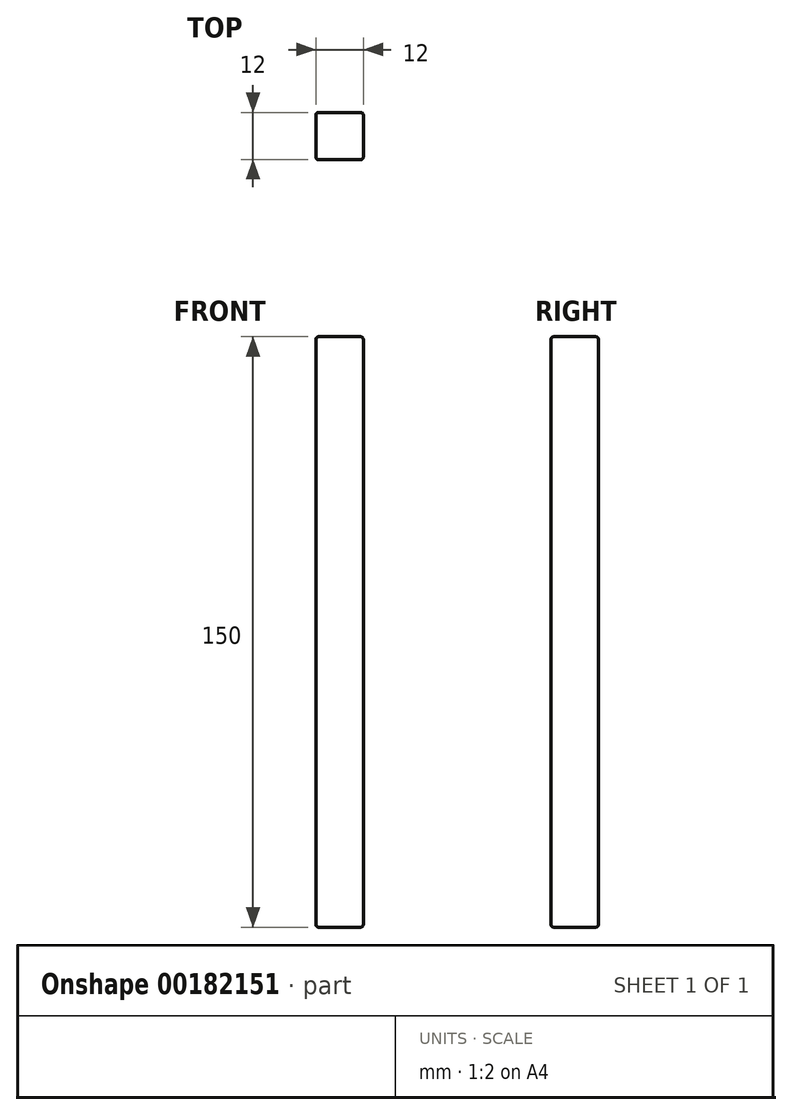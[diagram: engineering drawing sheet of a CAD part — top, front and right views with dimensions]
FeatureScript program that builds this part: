
annotation { "Feature Type Name" : "Feature", "Feature Type Description" : "" }
export const myFeature = defineFeature(function(context is Context, id is Id, definition is map)
    precondition{}
    {
        {
            var Q0;
            Q0=qCreatedBy(makeId("Top.planeOp"),FACE);
            var sketch = newSketch(context, id + "F0", { "sketchPlane" : qUnion([Q0])});
            skLineSegment(sketch, "E0.bottom", {"start": v(6, -6) * mm, "end": v(-6, -6) * mm});
            skLineSegment(sketch, "E0.top", {"start": v(6, 6) * mm, "end": v(-6, 6) * mm});
            skLineSegment(sketch, "E0.left", {"start": v(6, -6) * mm, "end": v(6, 6) * mm});
            skLineSegment(sketch, "E0.right", {"start": v(-6, -6) * mm, "end": v(-6, 6) * mm});
            skPoint(sketch, "E0.middle", {"position": v(0, 0) * mm});
            skSolve(sketch);
        }
        {
            var Q0;
            Q0 = qSketchRegion(id + "F0", true);
            extrude(context, id + "F1", {"entities" : qUnion([Q0]), "depth" : 150 * mm});
        }
        {
            var Q0;
            Q0=makeQuery(id+"F1.opExtrude","CAP_FACE",FACE,{"disambiguationData":[OSD([sQuery(id+"F0.wireOp",EDGE,"E0.bottom"),sQuery(id+"F0.wireOp",EDGE,"E0.top"),sQuery(id+"F0.wireOp",EDGE,"E0.left"),sQuery(id+"F0.wireOp",EDGE,"E0.right")])],"isStart":false});
            var Q1;
            Q1=makeQuery(id+"F1.opExtrude","SWEPT_FACE",FACE,{"disambiguationData":[OSD([sQuery(id+"F0.wireOp",EDGE,"E0.bottom")])]});
            var Q2;
            Q2=makeQuery(id+"F1.opExtrude","SWEPT_FACE",FACE,{"disambiguationData":[OSD([sQuery(id+"F0.wireOp",EDGE,"E0.left")])]});
            var Q3;
            Q3=makeQuery(id+"F1.opExtrude","SWEPT_FACE",FACE,{"disambiguationData":[OSD([sQuery(id+"F0.wireOp",EDGE,"E0.top")])]});
            var Q4;
            Q4=makeQuery(id+"F1.opExtrude","SWEPT_FACE",FACE,{"disambiguationData":[OSD([sQuery(id+"F0.wireOp",EDGE,"E0.right")])]});
            var Q5;
            Q5=makeQuery(id+"F1.opExtrude","CAP_FACE",FACE,{"disambiguationData":[OSD([sQuery(id+"F0.wireOp",EDGE,"E0.bottom"),sQuery(id+"F0.wireOp",EDGE,"E0.top"),sQuery(id+"F0.wireOp",EDGE,"E0.left"),sQuery(id+"F0.wireOp",EDGE,"E0.right")])],"isStart":true});
            fillet(context, id + "F2", {"entities" : qUnion([Q0, Q1, Q2, Q3, Q4, Q5]), "radius" : 0.6 * mm, "tangentPropagation" : true, "allowEdgeOverflow" : false});
        }
    });
